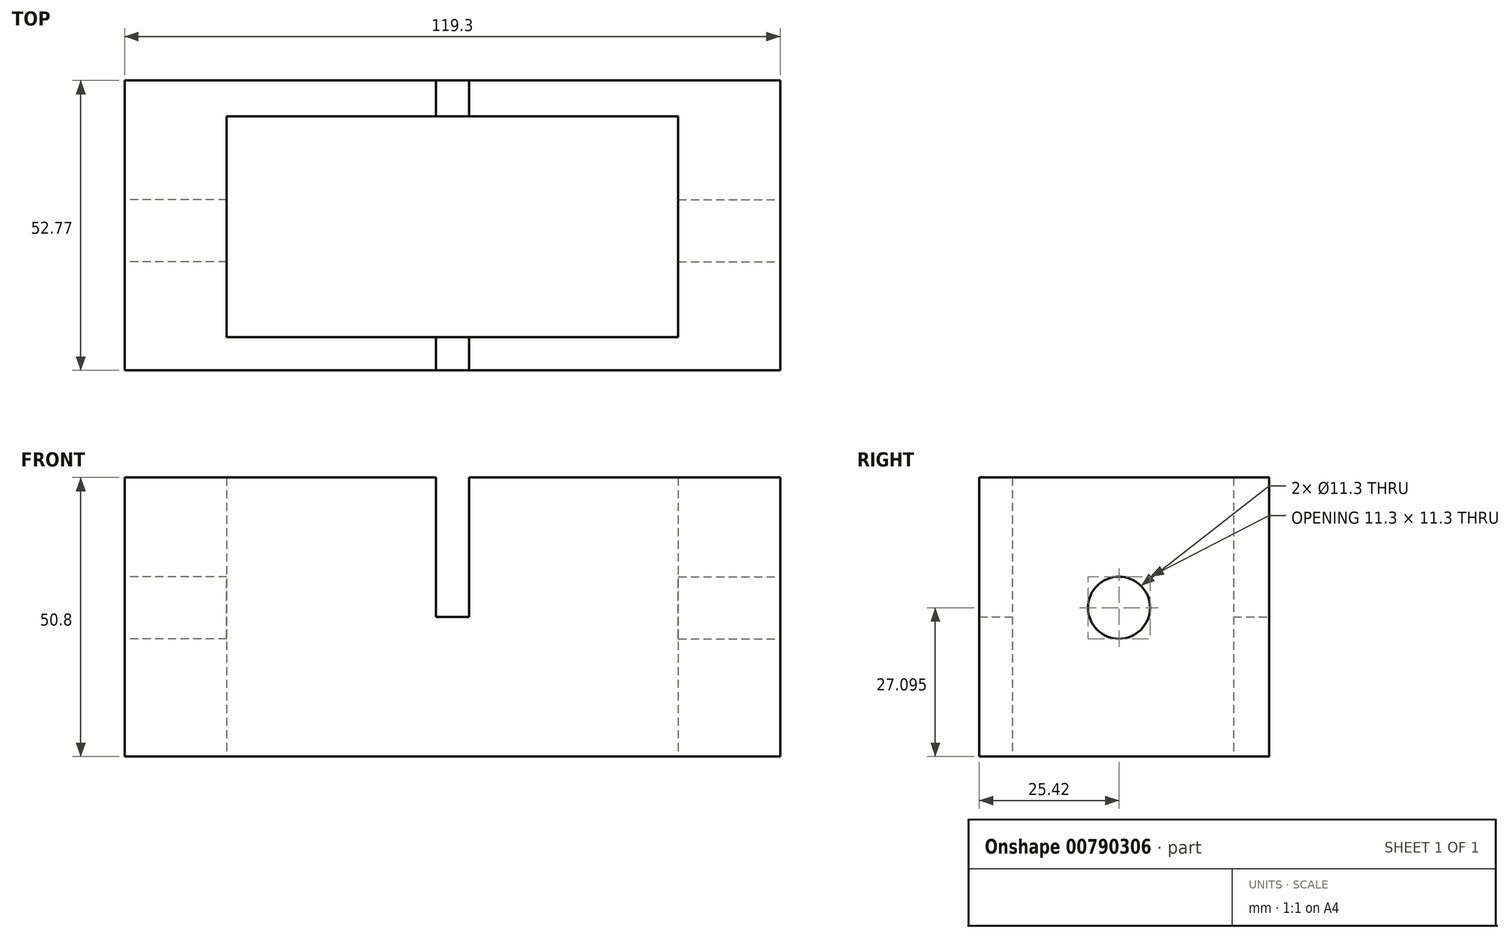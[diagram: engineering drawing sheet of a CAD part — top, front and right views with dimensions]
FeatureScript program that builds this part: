
annotation { "Feature Type Name" : "Feature", "Feature Type Description" : "" }
export const myFeature = defineFeature(function(context is Context, id is Id, definition is map)
    precondition{}
    {
        {
            var Q0;
            Q0=qCreatedBy(makeId("Top.planeOp"),FACE);
            var sketch = newSketch(context, id + "F0", { "sketchPlane" : qUnion([Q0])});
            skLineSegment(sketch, "E0.bottom", {"start": v(-59.65, 27.35) * mm, "end": v(-3.01, 27.35) * mm});
            skLineSegment(sketch, "E0.top", {"start": v(-59.65, 20.85) * mm, "end": v(-3.01, 20.85) * mm});
            skLineSegment(sketch, "E0.left", {"start": v(-59.65, 27.35) * mm, "end": v(-59.65, 20.85) * mm});
            skLineSegment(sketch, "E0.right", {"start": v(-3.01, 27.35) * mm, "end": v(-3.01, 20.85) * mm});
            skLineSegment(sketch, "E1.bottom", {"start": v(-59.65, 27.35) * mm, "end": v(-41.09, 27.35) * mm});
            skLineSegment(sketch, "E1.top", {"start": v(-59.65, -25.42) * mm, "end": v(-41.09, -25.42) * mm});
            skLineSegment(sketch, "E1.left", {"start": v(-59.65, 27.35) * mm, "end": v(-59.65, -25.42) * mm});
            skLineSegment(sketch, "E1.right", {"start": v(-41.09, 27.35) * mm, "end": v(-41.09, -25.42) * mm});
            skLineSegment(sketch, "E2.bottom", {"start": v(-59.65, -25.42) * mm, "end": v(-3.01, -25.42) * mm});
            skLineSegment(sketch, "E2.top", {"start": v(-59.65, -19.4) * mm, "end": v(-3.01, -19.4) * mm});
            skLineSegment(sketch, "E2.left", {"start": v(-59.65, -25.42) * mm, "end": v(-59.65, -19.4) * mm});
            skLineSegment(sketch, "E2.right", {"start": v(-3.01, -25.42) * mm, "end": v(-3.01, -19.4) * mm});
            skSolve(sketch);
        }
        {
            var Q0;
            Q0 = qSketchRegion(id + "F0", true);
            extrude(context, id + "F1", {"entities" : qUnion([Q0]), "depth" : 50.8 * mm, "offsetDistance" : 25.4 * mm});
        }
        {
            var Q0;
            Q0=makeQuery(id+"F1.opExtrude","SWEPT_FACE",FACE,{"disambiguationData":[OSD([sQuery(id+"F0.wireOp",EDGE,"E1.left"),sQuery(id+"F0.wireOp",EDGE,"E2.left")])]});
            var sketch = newSketch(context, id + "F2", { "sketchPlane" : qUnion([Q0])});
            skCircle(sketch, "E3", {"center": v(0, 27.1) * mm, "radius": 5.65 * mm});
            skSolve(sketch);
        }
        {
            var Q0;
            Q0=makeQuery(id+"F2.imprint","IMPRINT",FACE,{"disambiguationData":[TD([[makeQuery(id+"F2.imprint","IMPRINT",EDGE,{"derivedFrom":sQuery(id+"F2.wireOp",EDGE,"E3")}),1.0]])]});
            extrude(context, id + "F3", {"entities" : qUnion([Q0]), "operationType" : NewBodyOperationType.REMOVE, "oppositeDirection" : true, "depth" : 170.7 * mm, "offsetDistance" : 25.4 * mm});
        }
        {
            var Q0;
            Q0=makeQuery(id+"F1.opExtrude","SWEPT_FACE",FACE,{"disambiguationData":[OSD([sQuery(id+"F0.wireOp",EDGE,"E2.right")])]});
            var sketch = newSketch(context, id + "F4", { "sketchPlane" : qUnion([Q0])});
            skLineSegment(sketch, "E4", {"start": v(-25.42, 25.4) * mm, "end": v(-19.4, 25.4) * mm});
            skSolve(sketch);
        }
        {
            var Q0;
            {var subQ0=sQuery(id+"F4.wireOp",EDGE,"E4");Q0=makeQuery(id+"F4.imprint","IMPRINT",FACE,{"disambiguationData":[TD([[makeQuery(id+"F4.imprint","IMPRINT",EDGE,{"derivedFrom":subQ0}),-1.0]])]});}
            extrude(context, id + "F5", {"entities" : qUnion([Q0]), "operationType" : NewBodyOperationType.ADD, "depth" : 25.4 * mm, "offsetDistance" : 25.4 * mm});
        }
        {
            var Q0;
            Q0=makeQuery(id+"F1.opExtrude","SWEPT_FACE",FACE,{"disambiguationData":[OSD([sQuery(id+"F0.wireOp",EDGE,"E0.right")])]});
            var sketch = newSketch(context, id + "F6", { "sketchPlane" : qUnion([Q0])});
            skLineSegment(sketch, "E5", {"start": v(20.85, 25.4) * mm, "end": v(27.35, 25.4) * mm});
            skSolve(sketch);
        }
        {
            var Q0;
            Q0 = qSketchRegion(id + "F6", true);
            var Q1;
            {var subQ0=sQuery(id+"F6.wireOp",EDGE,"E5");Q1=makeQuery(id+"F6.imprint","IMPRINT",FACE,{"disambiguationData":[TD([[makeQuery(id+"F6.imprint","IMPRINT",EDGE,{"derivedFrom":subQ0}),-1.0]])]});}
            extrude(context, id + "F7", {"entities" : qUnion([Q0, Q1]), "operationType" : NewBodyOperationType.ADD, "depth" : 25.4 * mm, "offsetDistance" : 25.4 * mm});
        }
        {
            var Q0;
            Q0=makeQuery(id+"F1.opExtrude","SWEPT_BODY",BODY,{"disambiguationData":[OSD([sQuery(id+"F0.wireOp",EDGE,"E0.bottom"),sQuery(id+"F0.wireOp",EDGE,"E0.top"),sQuery(id+"F0.wireOp",EDGE,"E0.right"),sQuery(id+"F0.wireOp",EDGE,"E1.bottom"),sQuery(id+"F0.wireOp",EDGE,"E1.left"),sQuery(id+"F0.wireOp",EDGE,"E1.right"),sQuery(id+"F0.wireOp",EDGE,"E2.bottom"),sQuery(id+"F0.wireOp",EDGE,"E2.top"),sQuery(id+"F0.wireOp",EDGE,"E2.left"),sQuery(id+"F0.wireOp",EDGE,"E2.right")])]});
            var Q1;
            Q1=qCreatedBy(makeId("Right.planeOp"),FACE);
            mirror(context, id + "F8", {"operationType" : NewBodyOperationType.ADD, "entities" : qUnion([Q0]), "mirrorPlane" : qUnion([Q1])});
        }
    });
